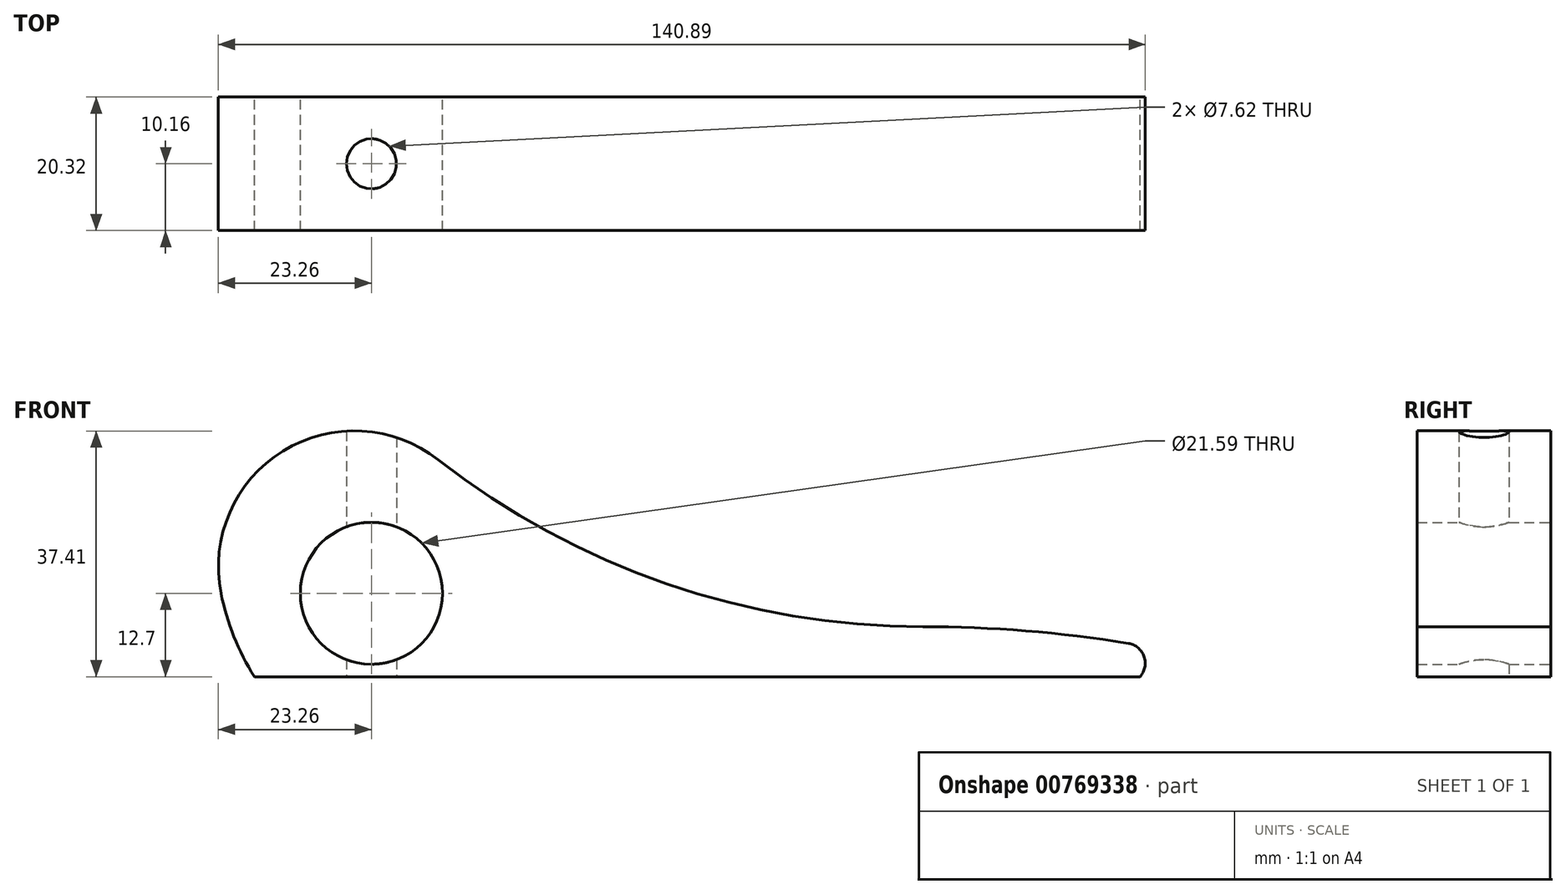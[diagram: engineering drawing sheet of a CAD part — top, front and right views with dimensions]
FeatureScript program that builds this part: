
annotation { "Feature Type Name" : "Feature", "Feature Type Description" : "" }
export const myFeature = defineFeature(function(context is Context, id is Id, definition is map)
    precondition{}
    {
        {
            var Q0;
            Q0=qCreatedBy(makeId("Front.planeOp"),FACE);
            var sketch = newSketch(context, id + "F0", { "sketchPlane" : qUnion([Q0])});
            skLineSegment(sketch, "E0", {"start": v(0, 0) * mm, "end": v(134.62, 0) * mm});
            skCircle(sketch, "E1", {"center": v(17.78, 12.7) * mm, "radius": 10.8 * mm});
            skArc(sketch, "E2", {"start": v(27.94, 33.02) * mm, "mid": v(62.64, 14.15) * mm, "end": v(101.6, 7.62) * mm});
            skLineSegment(sketch, "E3", {"start": v(65.73, 7.62) * mm, "end": v(94.5, 7.62) * mm, "construction": true});
            skArc(sketch, "E4", {"start": v(101.6, 7.62) * mm, "mid": v(117.27, 6.98) * mm, "end": v(132.84, 5.08) * mm});
            skArc(sketch, "E5", {"start": v(132.84, 5.08) * mm, "mid": v(135.24, 3.07) * mm, "end": v(134.62, 0) * mm});
            skArc(sketch, "E6", {"start": v(27.94, 33.02) * mm, "mid": v(4.36, 34.35) * mm, "end": v(-5.08, 12.7) * mm});
            skArc(sketch, "E7", {"start": v(-5.08, 12.7) * mm, "mid": v(-3.13, 6.12) * mm, "end": v(0, 0) * mm});
            skSolve(sketch);
        }
        {
            var Q0;
            Q0 = qSketchRegion(id + "F0", true);
            extrude(context, id + "F1", {"entities" : qUnion([Q0]), "depth" : 20.32 * mm, "offsetDistance" : 25.4 * mm});
        }
        {
            var Q0;
            Q0=makeQuery(id+"F1.opExtrude","SWEPT_FACE",FACE,{"disambiguationData":[OSD([sQuery(id+"F0.wireOp",EDGE,"E0")])]});
            var sketch = newSketch(context, id + "F2", { "sketchPlane" : qUnion([Q0])});
            skCircle(sketch, "E8", {"center": v(17.78, 10.16) * mm, "radius": 3.81 * mm});
            skPoint(sketch, "E8.centerSnap0", {"position": v(0, 10.16) * mm});
            skPoint(sketch, "E9.0", {"position": v(17.78, 0) * mm});
            skLineSegment(sketch, "E10", {"start": v(17.78, 0) * mm, "end": v(17.78, 20.32) * mm});
            skSolve(sketch);
        }
        {
            var Q0;
            {var subQ0=sQuery(id+"F2.wireOp",EDGE,"E10");var subQ1=sQuery(id+"F2.wireOp",EDGE,"E8");var subQ2=makeQuery(id+"F2.imprint","INTERSECT",VERTEX,{"disambiguationData":[OD(0.0)],"derivedFrom":[subQ1,subQ0]});Q0=makeQuery(id+"F2.imprint","IMPRINT",FACE,{"disambiguationData":[TD([[makeQuery(id+"F2.imprint","IMPRINT",EDGE,{"disambiguationData":[TD([[subQ2,-1.0]])],"derivedFrom":subQ1}),1.0]])]});}
            var Q1;
            {var subQ0=sQuery(id+"F2.wireOp",EDGE,"E10");var subQ1=sQuery(id+"F2.wireOp",EDGE,"E8");var subQ2=makeQuery(id+"F2.imprint","INTERSECT",VERTEX,{"disambiguationData":[OD(0.0)],"derivedFrom":[subQ1,subQ0]});Q1=makeQuery(id+"F2.imprint","IMPRINT",FACE,{"disambiguationData":[TD([[makeQuery(id+"F2.imprint","IMPRINT",EDGE,{"disambiguationData":[TD([[subQ2,1.0]])],"derivedFrom":subQ1}),1.0]])]});}
            extrude(context, id + "F3", {"entities" : qUnion([Q0, Q1]), "operationType" : NewBodyOperationType.REMOVE, "endBound" : BoundingType.THROUGH_ALL, "oppositeDirection" : true, "depth" : 25.4 * mm, "offsetDistance" : 25.4 * mm});
        }
    });
